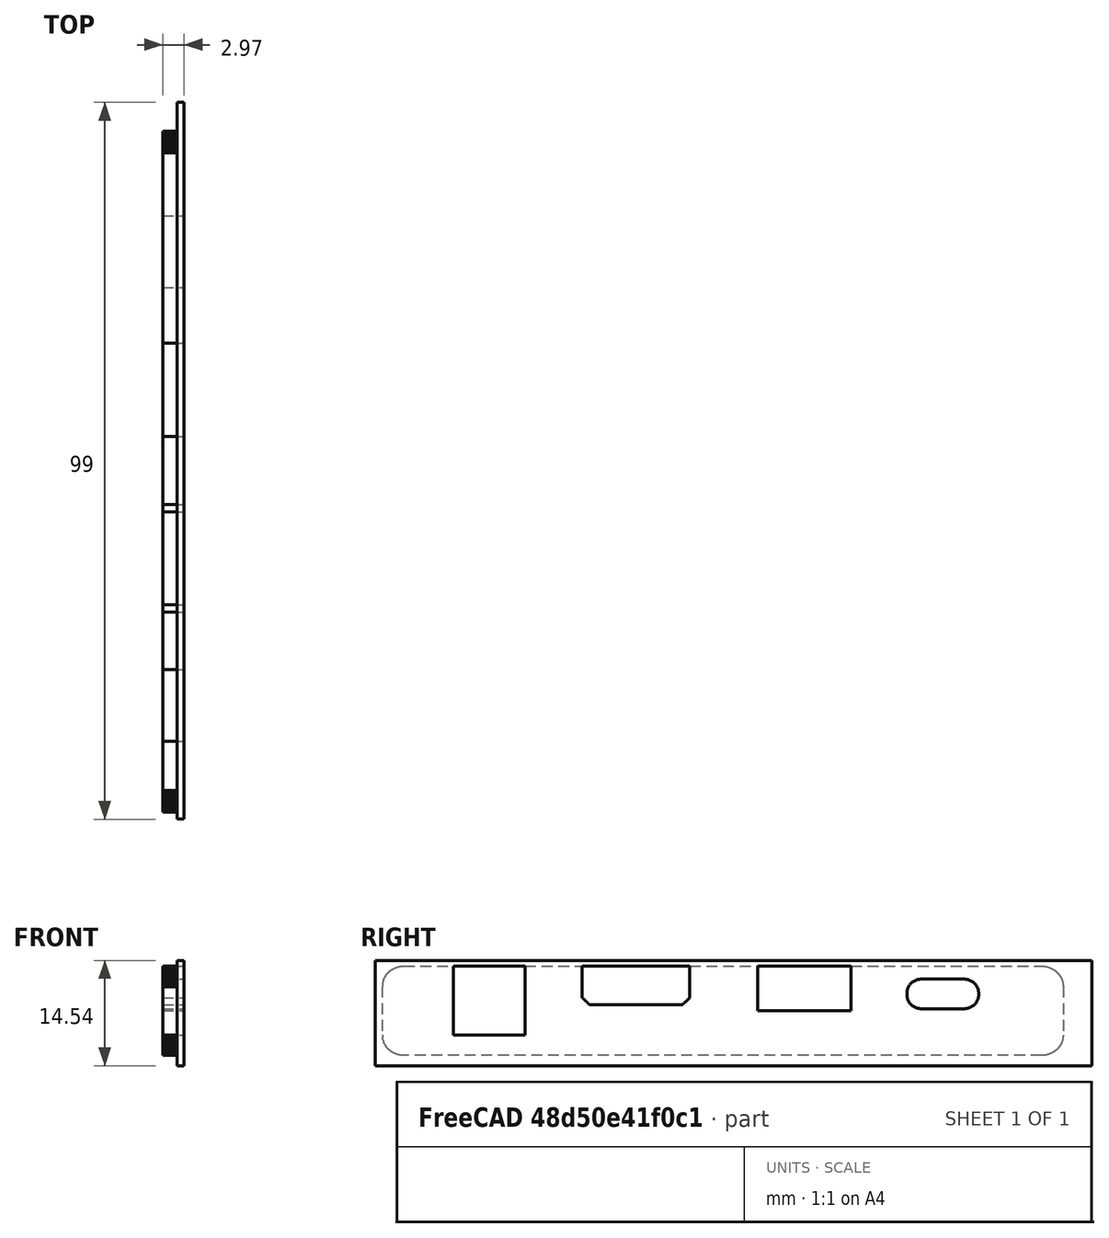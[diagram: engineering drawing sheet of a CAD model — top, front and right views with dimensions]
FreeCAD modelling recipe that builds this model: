
FCSTD DOCUMENT  (FreeCAD 0.21R33771 (Git))
Label: placa_puertos_A_Escala
License: All rights reserved
LicenseURL: http://en.wikipedia.org/wiki/All_rights_reserved
objects: Part::Box×5, Part::Cut×5, Mesh::Feature×1, Part::Feature×1, Part::Chamfer×1, Part::Fillet×1, Part::FeaturePython×1
note: 14 computed .brp shape members not serialized (recipe doc carries the construction recipe); baked Part::Feature solids carry a one-line shape summary decoded from their .brp

FEATURE [Mesh::Feature] CAJA_slimbook
FEATURE [Part::Box] Box  label="Cube"
  AttacherType = Attacher::AttachEngine3D
  Height = 15.3
  Length = 3
  Placement = pos=(-2,19,1.52) rot=(0,0,1;0rad)
  Width = 100
FEATURE [Part::Feature] Component018_solid  label="Component018 (Solid)"
  shape: bbox 239.2 x 150.2 x 25 mm, 4116 faces (baked)
FEATURE [Part::Cut] Cut
  Base = -> Box
  Placement = pos=(0,-0.4,-1) rot=(0,0,1;0rad)
  Refine = true
  Tool = -> Component018_solid
FEATURE [Part::Box] Box001  label="Cube001"
  AttacherType = Attacher::AttachEngine3D
  Height = 10
  Length = 10
  Placement = pos=(-7,29.5,5) rot=(0,0,1;0rad)
  Width = 10
FEATURE [Part::Box] Box002  label="Cube002"
  AttacherType = Attacher::AttachEngine3D
  Height = 5.6
  Length = 10
  Placement = pos=(-7,47.5,9.4) rot=(0,0,1;0rad)
  Width = 15
FEATURE [Part::Box] Box003  label="Cube003"
  AttacherType = Attacher::AttachEngine3D
  Height = 6.5
  Length = 12
  Placement = pos=(-7,72,8.5) rot=(0,0,1;0rad)
  Width = 13
FEATURE [Part::Box] Box004  label="Cube004"
  AttacherType = Attacher::AttachEngine3D
  Height = 4.3
  Length = 12
  Placement = pos=(-7,92.8,8.8) rot=(0,0,1;0rad)
  Width = 10
FEATURE [Part::Chamfer] Chamfer
  Base = -> Box002
  Edges = 2 edges r=1: [Edge9,Edge11]
FEATURE [Part::Fillet] Fillet
  Base = -> Box004
  Edges = 4 edges r=2: [Edge9,Edge10,Edge11,Edge12]
FEATURE [Part::Cut] Cut001
  Base = -> Cut
  Refine = true
  Tool = -> Box001
FEATURE [Part::Cut] Cut002
  Base = -> Cut001
  Refine = true
  Tool = -> Fillet
FEATURE [Part::Cut] Cut003
  Base = -> Cut002
  Refine = true
  Tool = -> Chamfer
FEATURE [Part::Cut] Cut004  label="placa-conectores-escala"
  Base = -> Cut003
  Placement = pos=(0,0.4,1) rot=(0,0,1;0rad)
  Refine = true
  Tool = -> Box003
FEATURE [Part::FeaturePython] Clone  label="Clon escalado_impresion"  # Draft clone (typed FeaturePython)
  AttacherType = Attacher::AttachEngine3D
  Fuse = false
  Objects = -> [Cut004]
  Placement = pos=(-0.02,1.05042,1.3503) rot=(0,0,1;0rad)
  Scale = (0.99,0.99,0.95)
